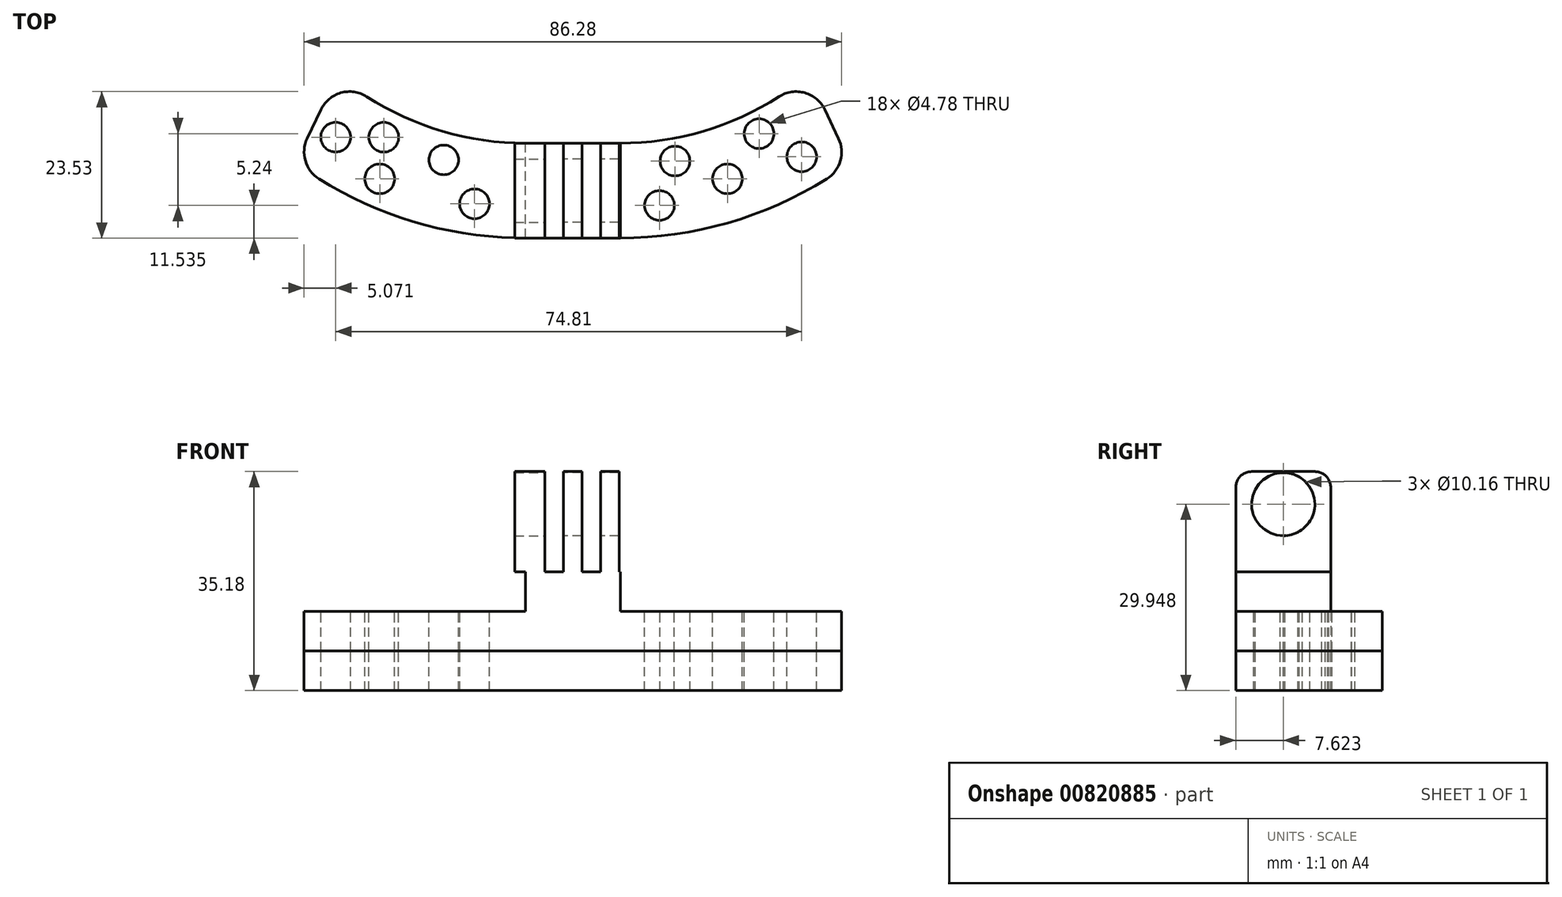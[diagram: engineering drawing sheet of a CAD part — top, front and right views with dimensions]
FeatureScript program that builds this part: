
annotation { "Feature Type Name" : "Feature", "Feature Type Description" : "" }
export const myFeature = defineFeature(function(context is Context, id is Id, definition is map)
    precondition{}
    {
        {
            var Q0;
            Q0=qCreatedBy(makeId("Top.planeOp"),FACE);
            var sketch = newSketch(context, id + "F0", { "sketchPlane" : qUnion([Q0])});
            skLineSegment(sketch, "E0", {"start": v(5.72, -9.52) * mm, "end": v(-9.52, -9.52) * mm});
            skLineSegment(sketch, "E1", {"start": v(-9.52, -9.52) * mm, "end": v(-9.52, 5.72) * mm});
            skLineSegment(sketch, "E2", {"start": v(-9.52, 5.72) * mm, "end": v(5.71, 5.72) * mm});
            skLineSegment(sketch, "E3", {"start": v(5.71, 5.72) * mm, "end": v(5.72, -9.52) * mm});
            skArc(sketch, "E4", {"start": v(-46.44, 2.56) * mm, "mid": v(-28.95, -6.42) * mm, "end": v(-9.52, -9.52) * mm});
            skArc(sketch, "E5", {"start": v(5.72, -9.52) * mm, "mid": v(25.13, -6.42) * mm, "end": v(42.62, 2.56) * mm});
            skArc(sketch, "E6", {"start": v(-39.7, 16.64) * mm, "mid": v(-25.57, 8.54) * mm, "end": v(-9.52, 5.72) * mm});
            skLineSegment(sketch, "E7", {"start": v(-39.7, 16.64) * mm, "end": v(-46.44, 2.56) * mm});
            skArc(sketch, "E8", {"start": v(5.71, 5.72) * mm, "mid": v(21.76, 8.53) * mm, "end": v(35.9, 16.64) * mm});
            skLineSegment(sketch, "E9", {"start": v(35.9, 16.64) * mm, "end": v(42.62, 2.56) * mm});
            skSolve(sketch);
        }
        {
            var Q0;
            Q0=makeQuery(id+"F0.imprint","IMPRINT",FACE,{"disambiguationData":[TD([[makeQuery(id+"F0.imprint","IMPRINT",EDGE,{"derivedFrom":sQuery(id+"F0.wireOp",EDGE,"E0")}),-1.0]])]});
            extrude(context, id + "F1", {"entities" : qUnion([Q0]), "depth" : 12.7 * mm, "offsetDistance" : 25.4 * mm});
        }
        {
            var Q0;
            Q0 = qSketchRegion(id + "F0", true);
            extrude(context, id + "F2", {"entities" : qUnion([Q0]), "operationType" : NewBodyOperationType.ADD, "depth" : 6.35 * mm, "offsetDistance" : 25.4 * mm});
        }
        {
            var Q0;
            Q0=makeQuery(id+"F2.opExtrude","SWEPT_EDGE",EDGE,{"disambiguationData":[OSD([sQuery(id+"F0.wireOp",EDGE,"E5"),sQuery(id+"F0.wireOp",EDGE,"E9")])]});
            var Q1;
            Q1=makeQuery(id+"F2.opExtrude","SWEPT_EDGE",EDGE,{"disambiguationData":[OSD([sQuery(id+"F0.wireOp",EDGE,"E8"),sQuery(id+"F0.wireOp",EDGE,"E9")])]});
            var Q2;
            Q2=makeQuery(id+"F2.opExtrude","SWEPT_EDGE",EDGE,{"disambiguationData":[OSD([sQuery(id+"F0.wireOp",EDGE,"E4"),sQuery(id+"F0.wireOp",EDGE,"E7")])]});
            var Q3;
            Q3=makeQuery(id+"F2.opExtrude","SWEPT_EDGE",EDGE,{"disambiguationData":[OSD([sQuery(id+"F0.wireOp",EDGE,"E6"),sQuery(id+"F0.wireOp",EDGE,"E7")])]});
            fillet(context, id + "F3", {"entities" : qUnion([Q0, Q1, Q2, Q3]), "radius" : 5.08 * mm, "tangentPropagation" : true, "allowEdgeOverflow" : false});
        }
        {
            var Q0;
            Q0=makeQuery(id+"F1.opExtrude","CAP_FACE",FACE,{"disambiguationData":[OSD([sQuery(id+"F0.wireOp",EDGE,"E0"),sQuery(id+"F0.wireOp",EDGE,"E1"),sQuery(id+"F0.wireOp",EDGE,"E2"),sQuery(id+"F0.wireOp",EDGE,"E3")])],"isStart":false});
            var sketch = newSketch(context, id + "F4", { "sketchPlane" : qUnion([Q0])});
            skLineSegment(sketch, "E10", {"start": v(-9.52, 5.72) * mm, "end": v(-9.35, 5.72) * mm});
            skLineSegment(sketch, "E11", {"start": v(-9.35, 5.72) * mm, "end": v(-9.35, -9.52) * mm});
            skLineSegment(sketch, "E12", {"start": v(-9.35, -9.52) * mm, "end": v(-6.38, -9.52) * mm});
            skLineSegment(sketch, "E13", {"start": v(-6.38, -9.52) * mm, "end": v(-6.37, 5.72) * mm});
            skLineSegment(sketch, "E14", {"start": v(-6.37, 5.72) * mm, "end": v(-9.35, 5.72) * mm});
            skLineSegment(sketch, "E15", {"start": v(-6.37, 5.72) * mm, "end": v(-3.4, 5.72) * mm});
            skLineSegment(sketch, "E16", {"start": v(5.71, 5.72) * mm, "end": v(5.54, 5.72) * mm});
            skLineSegment(sketch, "E17", {"start": v(-3.4, 5.72) * mm, "end": v(-0.43, 5.72) * mm});
            skLineSegment(sketch, "E18", {"start": v(-0.43, 5.72) * mm, "end": v(2.54, 5.72) * mm});
            skLineSegment(sketch, "E19", {"start": v(2.54, 5.72) * mm, "end": v(5.54, 5.72) * mm});
            skLineSegment(sketch, "E20", {"start": v(-3.4, 5.72) * mm, "end": v(-3.4, -9.52) * mm});
            skLineSegment(sketch, "E21", {"start": v(-0.43, 5.72) * mm, "end": v(-0.43, -9.52) * mm});
            skLineSegment(sketch, "E22", {"start": v(-0.43, -9.52) * mm, "end": v(-3.4, -9.52) * mm});
            skLineSegment(sketch, "E23", {"start": v(5.54, 5.72) * mm, "end": v(5.54, -9.52) * mm});
            skLineSegment(sketch, "E24", {"start": v(2.54, 5.72) * mm, "end": v(2.54, -9.52) * mm});
            skLineSegment(sketch, "E25", {"start": v(2.54, -9.52) * mm, "end": v(5.54, -9.52) * mm});
            skSolve(sketch);
        }
        {
            var Q0;
            Q0=makeQuery(id+"F4.imprint","IMPRINT",FACE,{"disambiguationData":[TD([[makeQuery(id+"F4.imprint","IMPRINT",EDGE,{"derivedFrom":sQuery(id+"F4.wireOp",EDGE,"E11")}),1.0]])]});
            var Q1;
            Q1=makeQuery(id+"F4.imprint","IMPRINT",FACE,{"disambiguationData":[TD([[makeQuery(id+"F4.imprint","IMPRINT",EDGE,{"derivedFrom":sQuery(id+"F4.wireOp",EDGE,"E17")}),-1.0]])]});
            var Q2;
            Q2=makeQuery(id+"F4.imprint","IMPRINT",FACE,{"disambiguationData":[TD([[makeQuery(id+"F4.imprint","IMPRINT",EDGE,{"derivedFrom":sQuery(id+"F4.wireOp",EDGE,"E19")}),-1.0]])]});
            extrude(context, id + "F5", {"entities" : qUnion([Q0, Q1, Q2]), "operationType" : NewBodyOperationType.ADD, "depth" : 16.13 * mm, "offsetDistance" : 25.4 * mm});
        }
        {
            var Q0;
            Q0=makeQuery(id+"F5.opExtrude","CAP_EDGE",EDGE,{"disambiguationData":[OSD([sQuery(id+"F4.wireOp",EDGE,"E12")])],"isStart":false});
            var Q1;
            Q1=makeQuery(id+"F5.opExtrude","CAP_EDGE",EDGE,{"disambiguationData":[OSD([sQuery(id+"F4.wireOp",EDGE,"E22")])],"isStart":false});
            var Q2;
            Q2=makeQuery(id+"F5.opExtrude","CAP_EDGE",EDGE,{"disambiguationData":[OSD([sQuery(id+"F4.wireOp",EDGE,"E25")])],"isStart":false});
            var Q3;
            Q3=makeQuery(id+"F5.opExtrude","CAP_EDGE",EDGE,{"disambiguationData":[OSD([sQuery(id+"F4.wireOp",EDGE,"E14")])],"isStart":false});
            var Q4;
            Q4=makeQuery(id+"F5.opExtrude","CAP_EDGE",EDGE,{"disambiguationData":[OSD([sQuery(id+"F4.wireOp",EDGE,"E17")])],"isStart":false});
            var Q5;
            Q5=makeQuery(id+"F5.opExtrude","CAP_EDGE",EDGE,{"disambiguationData":[OSD([sQuery(id+"F4.wireOp",EDGE,"E19")])],"isStart":false});
            fillet(context, id + "F6", {"entities" : qUnion([Q0, Q1, Q2, Q3, Q4, Q5]), "radius" : 2.54 * mm, "tangentPropagation" : true, "allowEdgeOverflow" : false});
        }
        {
            var Q0;
            Q0=makeQuery(id+"F5.opExtrude","SWEPT_FACE",FACE,{"disambiguationData":[OSD([sQuery(id+"F4.wireOp",EDGE,"E11")])]});
            var sketch = newSketch(context, id + "F7", { "sketchPlane" : qUnion([Q0])});
            skLineSegment(sketch, "E26", {"start": v(1.9, 28.83) * mm, "end": v(1.9, 12.7) * mm});
            skCircle(sketch, "E27", {"center": v(1.9, 23.6) * mm, "radius": 2.68 * mm});
            skCircle(sketch, "E28", {"center": v(1.9, 23.6) * mm, "radius": 5.08 * mm});
            skSolve(sketch);
        }
        {
            var Q0;
            {var subQ0=sQuery(id+"F7.wireOp",EDGE,"E28");var subQ1=sQuery(id+"F7.wireOp",EDGE,"E26");var subQ2=makeQuery(id+"F7.imprint","INTERSECT",VERTEX,{"disambiguationData":[OD(0.0)],"derivedFrom":[subQ1,subQ0]});Q0=makeQuery(id+"F7.imprint","IMPRINT",FACE,{"disambiguationData":[TD([[makeQuery(id+"F7.imprint","IMPRINT",EDGE,{"disambiguationData":[TD([[subQ2,-1.0]])],"derivedFrom":subQ1}),1.0]])]});}
            var Q1;
            {var subQ0=sQuery(id+"F7.wireOp",EDGE,"E28");var subQ1=sQuery(id+"F7.wireOp",EDGE,"E26");var subQ2=makeQuery(id+"F7.imprint","INTERSECT",VERTEX,{"disambiguationData":[OD(0.0)],"derivedFrom":[subQ1,subQ0]});Q1=makeQuery(id+"F7.imprint","IMPRINT",FACE,{"disambiguationData":[TD([[makeQuery(id+"F7.imprint","IMPRINT",EDGE,{"disambiguationData":[TD([[subQ2,-1.0]])],"derivedFrom":subQ1}),-1.0]])]});}
            extrude(context, id + "F8", {"entities" : qUnion([Q0, Q1]), "operationType" : NewBodyOperationType.ADD, "depth" : 1.9 * mm, "offsetDistance" : 25.4 * mm});
        }
        {
            var Q0;
            Q0=makeQuery(id+"F8.boolean.opBoolean","SPLIT",FACE,{"disambiguationData":[TD([makeQuery(id+"F8.opExtrude","SWEPT_FACE",FACE,{"disambiguationData":[OSD([sQuery(id+"F7.wireOp",EDGE,"E27")])]})])],"derivedFrom":makeQuery(id+"F5.opExtrude","SWEPT_FACE",FACE,{"disambiguationData":[OSD([sQuery(id+"F4.wireOp",EDGE,"E11")])]})});
            extrude(context, id + "F9", {"entities" : qUnion([Q0]), "operationType" : NewBodyOperationType.REMOVE, "oppositeDirection" : true, "depth" : 25.4 * mm, "offsetDistance" : 25.4 * mm});
        }
        {
            var Q0;
            Q0=makeQuery(id+"F0.imprint","IMPRINT",FACE,{"disambiguationData":[TD([[makeQuery(id+"F0.imprint","IMPRINT",EDGE,{"derivedFrom":sQuery(id+"F0.wireOp",EDGE,"E0")}),-1.0]])]});
            var Q1;
            Q1=makeQuery(id+"F0.imprint","IMPRINT",FACE,{"disambiguationData":[TD([[makeQuery(id+"F0.imprint","IMPRINT",EDGE,{"derivedFrom":sQuery(id+"F0.wireOp",EDGE,"E1")}),1.0]])]});
            var Q2;
            Q2=makeQuery(id+"F0.imprint","IMPRINT",FACE,{"disambiguationData":[TD([[makeQuery(id+"F0.imprint","IMPRINT",EDGE,{"derivedFrom":sQuery(id+"F0.wireOp",EDGE,"E3")}),1.0]])]});
            extrude(context, id + "F10", {"entities" : qUnion([Q0, Q1, Q2]), "oppositeDirection" : true, "depth" : 6.35 * mm, "offsetDistance" : 25.4 * mm});
        }
        {
            var Q0;
            Q0=makeQuery(id+"F10.opExtrude","SWEPT_EDGE",EDGE,{"disambiguationData":[OSD([sQuery(id+"F0.wireOp",EDGE,"E4"),sQuery(id+"F0.wireOp",EDGE,"E7")])]});
            var Q1;
            Q1=makeQuery(id+"F10.opExtrude","SWEPT_EDGE",EDGE,{"disambiguationData":[OSD([sQuery(id+"F0.wireOp",EDGE,"E5"),sQuery(id+"F0.wireOp",EDGE,"E9")])]});
            var Q2;
            Q2=makeQuery(id+"F10.opExtrude","SWEPT_EDGE",EDGE,{"disambiguationData":[OSD([sQuery(id+"F0.wireOp",EDGE,"E8"),sQuery(id+"F0.wireOp",EDGE,"E9")])]});
            var Q3;
            Q3=makeQuery(id+"F10.opExtrude","SWEPT_EDGE",EDGE,{"disambiguationData":[OSD([sQuery(id+"F0.wireOp",EDGE,"E6"),sQuery(id+"F0.wireOp",EDGE,"E7")])]});
            fillet(context, id + "F11", {"entities" : qUnion([Q0, Q1, Q2, Q3]), "radius" : 5.08 * mm, "tangentPropagation" : true, "allowEdgeOverflow" : false});
        }
        {
            var Q0;
            {var subQ0=sQuery(id+"F0.wireOp",EDGE,"E2");var subQ1=sQuery(id+"F0.wireOp",EDGE,"E4");var subQ2=sQuery(id+"F0.wireOp",EDGE,"E0");var subQ3=sQuery(id+"F0.wireOp",EDGE,"E7");var subQ4=sQuery(id+"F0.wireOp",EDGE,"E6");Q0=makeQuery(id+"F2.boolean.opBoolean","SPLIT",FACE,{"disambiguationData":[TD([makeQuery(id+"F1.opExtrude","SWEPT_FACE",FACE,{"disambiguationData":[OSD([sQuery(id+"F0.wireOp",EDGE,"E1")])]})])],"derivedFrom":makeQuery(id+"F2.opExtrude","CAP_FACE",FACE,{"disambiguationData":[OSD([subQ2,subQ0,subQ1,sQuery(id+"F0.wireOp",EDGE,"E5"),subQ4,subQ3,sQuery(id+"F0.wireOp",EDGE,"E8"),sQuery(id+"F0.wireOp",EDGE,"E9")])],"isStart":false})});}
            var sketch = newSketch(context, id + "F12", { "sketchPlane" : qUnion([Q0])});
            skCircle(sketch, "E29", {"center": v(-39.98, 6.69) * mm, "radius": 2.39 * mm});
            skCircle(sketch, "E30", {"center": v(-32.26, 6.68) * mm, "radius": 2.39 * mm});
            skCircle(sketch, "E31", {"center": v(-32.91, 0) * mm, "radius": 2.39 * mm});
            skCircle(sketch, "E32", {"center": v(-22.63, 3.04) * mm, "radius": 2.38 * mm});
            skCircle(sketch, "E33", {"center": v(-17.69, -4.02) * mm, "radius": 2.39 * mm});
            skCircle(sketch, "E34", {"center": v(12, -4.28) * mm, "radius": 2.39 * mm});
            skCircle(sketch, "E35", {"center": v(14.5, 2.86) * mm, "radius": 2.39 * mm});
            skCircle(sketch, "E36", {"center": v(22.9, 0) * mm, "radius": 2.39 * mm});
            skCircle(sketch, "E37", {"center": v(27.99, 7.26) * mm, "radius": 2.39 * mm});
            skCircle(sketch, "E38", {"center": v(34.83, 3.54) * mm, "radius": 2.39 * mm});
            skSolve(sketch);
        }
        {
            var Q0;
            Q0=makeQuery(id+"F12.imprint","IMPRINT",FACE,{"disambiguationData":[TD([[makeQuery(id+"F12.imprint","IMPRINT",EDGE,{"derivedFrom":sQuery(id+"F12.wireOp",EDGE,"E29")}),1.0]])]});
            var Q1;
            Q1=makeQuery(id+"F12.imprint","IMPRINT",FACE,{"disambiguationData":[TD([[makeQuery(id+"F12.imprint","IMPRINT",EDGE,{"derivedFrom":sQuery(id+"F12.wireOp",EDGE,"E30")}),1.0]])]});
            var Q2;
            Q2=makeQuery(id+"F12.imprint","IMPRINT",FACE,{"disambiguationData":[TD([[makeQuery(id+"F12.imprint","IMPRINT",EDGE,{"derivedFrom":sQuery(id+"F12.wireOp",EDGE,"E31")}),1.0]])]});
            var Q3;
            Q3=makeQuery(id+"F12.imprint","IMPRINT",FACE,{"disambiguationData":[TD([[makeQuery(id+"F12.imprint","IMPRINT",EDGE,{"derivedFrom":sQuery(id+"F12.wireOp",EDGE,"E32")}),1.0]])]});
            var Q4;
            Q4=makeQuery(id+"F12.imprint","IMPRINT",FACE,{"disambiguationData":[TD([[makeQuery(id+"F12.imprint","IMPRINT",EDGE,{"derivedFrom":sQuery(id+"F12.wireOp",EDGE,"E33")}),1.0]])]});
            var Q5;
            Q5=makeQuery(id+"F12.imprint","IMPRINT",FACE,{"disambiguationData":[TD([[makeQuery(id+"F12.imprint","IMPRINT",EDGE,{"derivedFrom":sQuery(id+"F12.wireOp",EDGE,"E34")}),1.0]])]});
            var Q6;
            Q6=makeQuery(id+"F12.imprint","IMPRINT",FACE,{"disambiguationData":[TD([[makeQuery(id+"F12.imprint","IMPRINT",EDGE,{"derivedFrom":sQuery(id+"F12.wireOp",EDGE,"E35")}),1.0]])]});
            var Q7;
            Q7=makeQuery(id+"F12.imprint","IMPRINT",FACE,{"disambiguationData":[TD([[makeQuery(id+"F12.imprint","IMPRINT",EDGE,{"derivedFrom":sQuery(id+"F12.wireOp",EDGE,"E36")}),1.0]])]});
            var Q8;
            Q8=makeQuery(id+"F12.imprint","IMPRINT",FACE,{"disambiguationData":[TD([[makeQuery(id+"F12.imprint","IMPRINT",EDGE,{"derivedFrom":sQuery(id+"F12.wireOp",EDGE,"E37")}),1.0]])]});
            var Q9;
            Q9=makeQuery(id+"F12.imprint","IMPRINT",FACE,{"disambiguationData":[TD([[makeQuery(id+"F12.imprint","IMPRINT",EDGE,{"derivedFrom":sQuery(id+"F12.wireOp",EDGE,"E38")}),1.0]])]});
            extrude(context, id + "F13", {"entities" : qUnion([Q0, Q1, Q2, Q3, Q4, Q5, Q6, Q7, Q8, Q9]), "operationType" : NewBodyOperationType.REMOVE, "oppositeDirection" : true, "depth" : 25.4 * mm, "offsetDistance" : 25.4 * mm});
        }
    });
